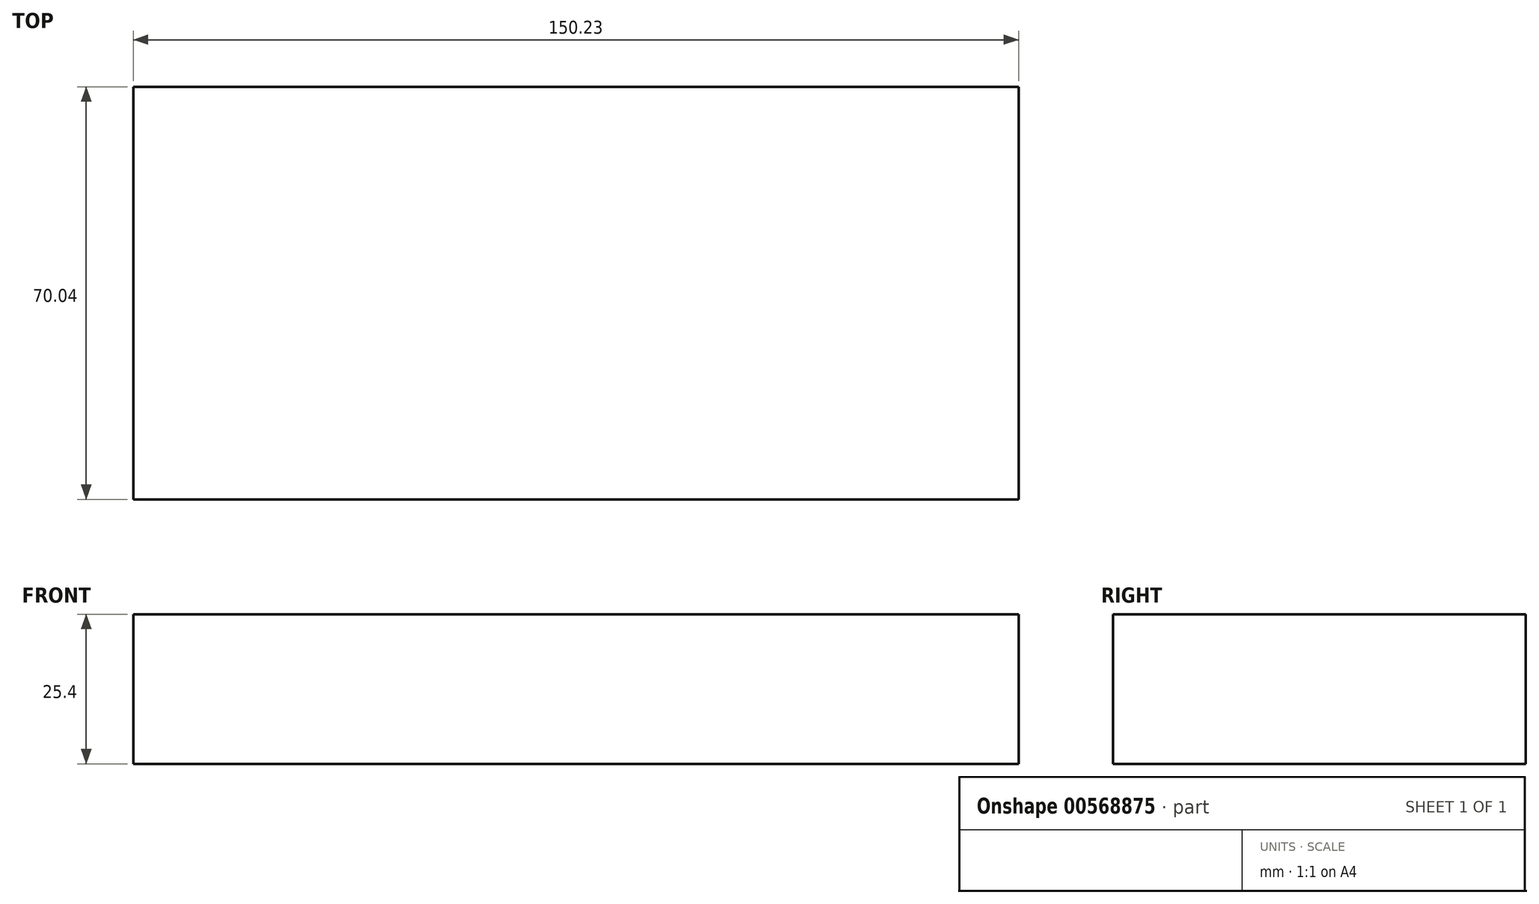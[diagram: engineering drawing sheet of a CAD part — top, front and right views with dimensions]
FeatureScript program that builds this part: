
annotation { "Feature Type Name" : "Feature", "Feature Type Description" : "" }
export const myFeature = defineFeature(function(context is Context, id is Id, definition is map)
    precondition{}
    {
        {
            var Q0;
            Q0=qCreatedBy(makeId("Top.planeOp"),FACE);
            var sketch = newSketch(context, id + "F0", { "sketchPlane" : qUnion([Q0])});
            skLineSegment(sketch, "E0.bottom", {"start": v(0, 0) * mm, "end": v(-150.23, 0) * mm});
            skLineSegment(sketch, "E0.top", {"start": v(0, 70.04) * mm, "end": v(-150.23, 70.04) * mm});
            skLineSegment(sketch, "E0.left", {"start": v(0, 0) * mm, "end": v(0, 70.04) * mm});
            skLineSegment(sketch, "E0.right", {"start": v(-150.23, 0) * mm, "end": v(-150.23, 70.04) * mm});
            skSolve(sketch);
        }
        {
            var Q0;
            Q0 = qSketchRegion(id + "F0", true);
            extrude(context, id + "F1", {"entities" : qUnion([Q0]), "depth" : 25.4 * mm, "offsetDistance" : 25.4 * mm});
        }
    });
